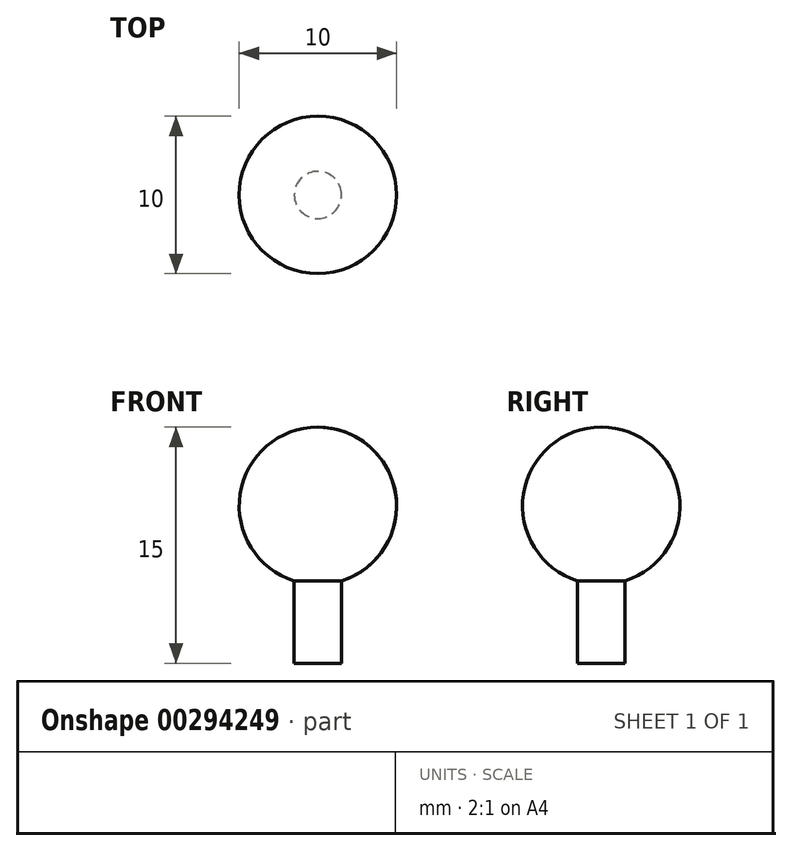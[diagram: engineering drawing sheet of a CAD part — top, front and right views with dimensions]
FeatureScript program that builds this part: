
annotation { "Feature Type Name" : "Feature", "Feature Type Description" : "" }
export const myFeature = defineFeature(function(context is Context, id is Id, definition is map)
    precondition{}
    {
        {
            var Q0;
            Q0=qCreatedBy(makeId("Front.planeOp"),FACE);
            var sketch = newSketch(context, id + "F0", { "sketchPlane" : qUnion([Q0])});
            skArc(sketch, "E0", {"start": v(1.5, -4.77) * mm, "mid": v(4.94, 0.76) * mm, "end": v(0, 5) * mm});
            skLineSegment(sketch, "E1.top", {"start": v(0, -10) * mm, "end": v(1.5, -10) * mm});
            skLineSegment(sketch, "E1.right", {"start": v(1.5, -4.77) * mm, "end": v(1.5, -10) * mm});
            skPoint(sketch, "E2.orphan", {"position": v(-1.5, 10) * mm});
            skPoint(sketch, "E3.orphan", {"position": v(1.5, 10) * mm});
            skLineSegment(sketch, "E4", {"start": v(0, 0) * mm, "end": v(0, -10) * mm});
            skLineSegment(sketch, "E5", {"start": v(0, 5) * mm, "end": v(0, 0) * mm});
            skPoint(sketch, "E6.orphan", {"position": v(-1.5, -10) * mm});
            skSolve(sketch);
        }
        {
            var Q0;
            Q0 = qSketchRegion(id + "F0", true);
            var Q1;
            Q1=sQuery(id+"F0.wireOp",EDGE,"E4");
            revolve(context, id + "F1", {"entities" : qUnion([Q0]), "axis" : qUnion([Q1]), "revolveType" : RevolveType.FULL});
        }
    });
